# Revit family: DTI30M977BB_Revit
name_source: partatom
category: Specialty Equipment
revit_build: Autodesk Revit MEP 2014 (Build: 20130308_1515(x64)
units: mm (PartAtom-declared; Revit-internal decimal feet)

## types (1)
- DTI30M977BB
    AUTO PAN DETECTION = YES
    BLUETOOTH CONNECT = YES
    CENTER HEATING ELEMENT = 7”/11” POWER COIL™ (VF)
    CHILD LOCK = YES
    CIRCUIT BREAKER (A) = 40
    DEMO MODE = YES
    Depth = 21 1/4"
    Description = 30-INCH INDUCTION COOKTOP MODERNIST COLLECTION
    ENERGY SOURCE = ELECTRIC
    FLEX ZONE LEFT = 7 19/20”W X 15 6/25”D
    FLEX ZONE LEFT FRONT (W) = 1800W / 2600W (B)
    FLEX ZONE LEFT REAR (W) = 1800W / 2600W (B)
    FLEX ZONE POWER = 3300W / 3600W (B)
    FLEX ZONE RIGHT = 7 19/20”W X 15 6/25”D
    FLEX ZONE RIGHT REAR (W) = 1400W / 1800W (B)
    FREQUENCY (HZ) = 60
    GUIDED COOKING = YES - 15 EA
    HOOD CONNECTIVITY ON/OFF = YES
    Height = 4"
    KITCHEN TIMER = YES
    LIMITED, PARTS AND LABOR = 1 YEAR
    Manufacturer = Dacor
    Model = DTI30M977BB
    PAUSE = YES
    POWER COIL CENTER (W) = 3600W / 4800W (B)
    POWER LEVEL SETTING = 9 + POWER BOOST
    POWER ON/OFF = YES
    QUICK STOP = YES
    RECOMMENDED POWER LEVEL = YES
    RESIDUAL HEAT INDICATOR = 2 STAGE
    RIGHT REAR HEATING ELEMENT = 6” POWER COIL™ (VF)
    SIMMER/MELT = YES
    SOUND ON/OFF = YES
    Support = Plastic-Black
    TOTAL NUMBER OF COOKTOP ZONES = 6
    Unit = Stainless Steel
    VIRTUAL FLAME ON/OFF = YES
    VOLTS (V) = 240 / 208
    WATTS (W) = 10.8 KW / 9.5 KW
    WI FI CONNECT = YES
    Width = 30"
    ZONES WITH BOOSTER = 5

## geometry (parser evidence)
native form markers: Sweep x1
no freeform markers — native parametric forms only
